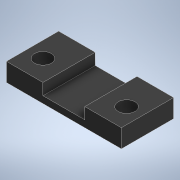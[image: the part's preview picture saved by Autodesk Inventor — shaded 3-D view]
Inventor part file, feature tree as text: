
AUTODESK INVENTOR PART (.ipt)
format: ipt  version: 2021 (Build 250183000, 183)  size: 121,856 bytes
history: native  units: mm
features: extrude x2, sketch x2
ambient origin geometry x8: Origin, YZ Plane, XZ Plane, XY Plane, X Axis, Y Axis, Z Axis, Center Point
bodies: Solid1 (feature_tree)
feature tree (4):
  extrude  "Extrusion1"  Depth=2.2mm
  extrude  "Extrusion2"  Depth=22.0mm
  sketch  "Sketch1"  dims[d0=8.0mm d1=2.2mm]
  sketch  "Sketch2"  dims[d2=3.5mm d3=22.0mm d4=10.0mm d5=0.0mm d6=6.0mm d7=16.0mm d8=8.0mm d9=3.2mm d10=0.0mm d11=0.0mm]
